# Revit family: HARMANN-Wentylator dachowy-VERT EC-Wywiewny
name_source: partatom
category: Wyposażenie mechaniczne
units: mm (PartAtom-declared; Revit-internal decimal feet)

## family parameters
Oparty na płaszczyźnie roboczej = Nie
Punkt obliczania pomieszczeń = Nie
Tnij formami wycięć po wczytaniu = Nie
Typ części = Normalny
Współdzielony = Nie
Wymiar okrągłego złącza = Użyj średnicy
Zachowaj orientację opisów = Nie
Zawsze pionowo = Tak

## types (3) — shared parameters
Domyślna rzędna = 0.0 mm
IfcExportAs = IfcFanType
IfcExportType = NOTDEFINED
Kod Producent = Harmann
Kod Typoszereg = VERT EC
Object Date = 2018.11.30
Object Destination = PL
Object ID = F000104RFAPL
Object Language = PL
Object Revit = 2017
Object Version = 1.00
Opis = Wentylator dachowy
Opt Akcesorium Podstawa A = ᴬ : Brak Podstawy
Opt Akcesorium Podstawa B = ᴬ : Podstawa Dachowa
Opt Akcesorium Podstawa C = ᴬ : Tłumiąca Podstawa Dachowa
Otoczenie Temperatura Maksymalna = 60.0 °C
Otoczenie Temperatura Minimalna = -30.0 °C
Powietrze Wywiewane Ciśnienie Statyczne Nominalne = 100.0 Pa
Powietrze Wywiewane Temperatura Maksymalna = 60.0 °C
Producent = Harmann Polska Sp. z o.o.
Producent Nazwa = Harmann Polska Sp. z o.o.
Prt Komponent A2 = VE-Zagnieżdżone-Akcesorium-ParaForma-Harmann-DAS-Złącze_Przeciwdrganiowe : 180
Prt Komponent A3 = VE-Zagnieżdżone-Akcesorium-ParaForma-Harmann-DVK-Przepustnica_Zwrotna : 180
Prt Komponent A4 = VE-Zagnieżdżone-Akcesorium-ParaForma-Harmann-DKP-Płyta_Adaptacyjna : 220
Prt Komponent A5 = VE-Zagnieżdżone-Akcesorium-ParaForma-Harmann-DSF_AL-Podstawa_Dachowa : 220
Prt Komponent A6 = VE-Zagnieżdżone-Akcesorium-ParaForma-Harmann-DSS_AL-Podstawa_Dachowa : 220
Systematyka Branża = Instalacje Sanitarne
Systematyka Dziedzina = Instalacje Wentylacyjne
Systematyka Klasa = Wentylator
Systematyka Rodzaj = Wentylator Dachowy
Zasilanie Częstotliwość Nominalna = 50 Hz
Zasilanie Ilość Faz = 1
Zasilanie Konfiguracja Uzwojeń = n/d
Zasilanie Napięcie Nominalne = 230 V
Zasilanie Natężenie = 1 A
Zasilanie Rodzaj Sterowania = Sterowanie napięciem 0-10V
ds = 220.0 mm
l1_a0 = 0.0 mm
l1_a1 = 0.0 mm
l1_a2 = 0.0 mm
l1_a3 = 0.0 mm
l1_a4 = 0.0 mm
l1_a5 = 320.0 mm
l1_a6 = 620.0 mm
l2_a0 = 0.0 mm
l2_a1 = 1.0 mm
l2_a2 = 155.0 mm
l2_a3 = 115.0 mm
l2_a4 = 1.0 mm
l2_a5 = 0.0 mm
l2_a6 = 0.0 mm
wx_a0 = 95.5 mm
wy_a0 = 95.5 mm
wz_a0 = 0.0 mm

## per-type parameters (varying)
| type | Kod Numer Katalogowy | Masa Netto | Otoczenie Poziom Ciśnienia Akustycznego Nominalny z 01 m | Otoczenie Poziom Ciśnienia Akustycznego Nominalny z 04 m | Otoczenie Poziom Ciśnienia Akustycznego Nominalny z 10 m | Otoczenie Poziom Mocy Akustycznej Nominalny Obudowa | Powietrze Wywiewane Ciśnienie Statyczne Maksymalne | Powietrze Wywiewane Poziom Mocy Akustycznej Nominalny Wlot | Powietrze Wywiewane Przepływ Maksymalny | Powietrze Wywiewane Przepływ Nominalny | Prt Komponent A1 | Prt Komponent N1 | Zasilanie Moc | Zasilanie Moc Pozorna | Zasilanie Współczynnik Mocy | dn | s1 |
| VERT 190/750 EC | 78252227 | 3.5 kg | 47 | 36 | 32 | 55 | 635.0 Pa | 60 | 750 m³/h | 250 m³/h | VE-Zagnieżdżone-Akcesorium-ParaForma-Harmann-DAF-Króciec_Przyłączeniowy : DRK 160 | GE-Komponent-ParaForma-Harmann-VIVER_EC-N1a : VERT 190/750 EC | 123 W | 207 VA | 0.594 | 160.0 mm | 160.0 mm |
| VERT 220/1050 EC | 78252300 | 3.5 kg | 44 | 33 | 29 | 52 | 1000.0 Pa | 51 | 1050 m³/h | 300 m³/h | VE-Zagnieżdżone-Akcesorium-ParaForma-Harmann-DAF-Króciec_Przyłączeniowy : DRK 160 | GE-Komponent-ParaForma-Harmann-VIVER_EC-N1a : VERT 220/1050EC | 175 W | 265 VA | 0.66 | 160.0 mm | 160.0 mm |
| VERT 250/1400 EC | 78135316 | 4.0 kg | 52 | 41 | 37 | 60 | 1050.0 Pa | 58 | 1400 m³/h | 500 m³/h | VE-Zagnieżdżone-Akcesorium-ParaForma-Harmann-DAF-Króciec_Przyłączeniowy : DRK 200 | GE-Komponent-ParaForma-Harmann-VIVER_EC-N1a : VERT 250/1400EC | 175 W | 265 VA | 0.66 | 200.0 mm | 200.0 mm |

note: column(s) folded — value = type name in every type: Kod Zamówienia, Model, Opis indeksowy
